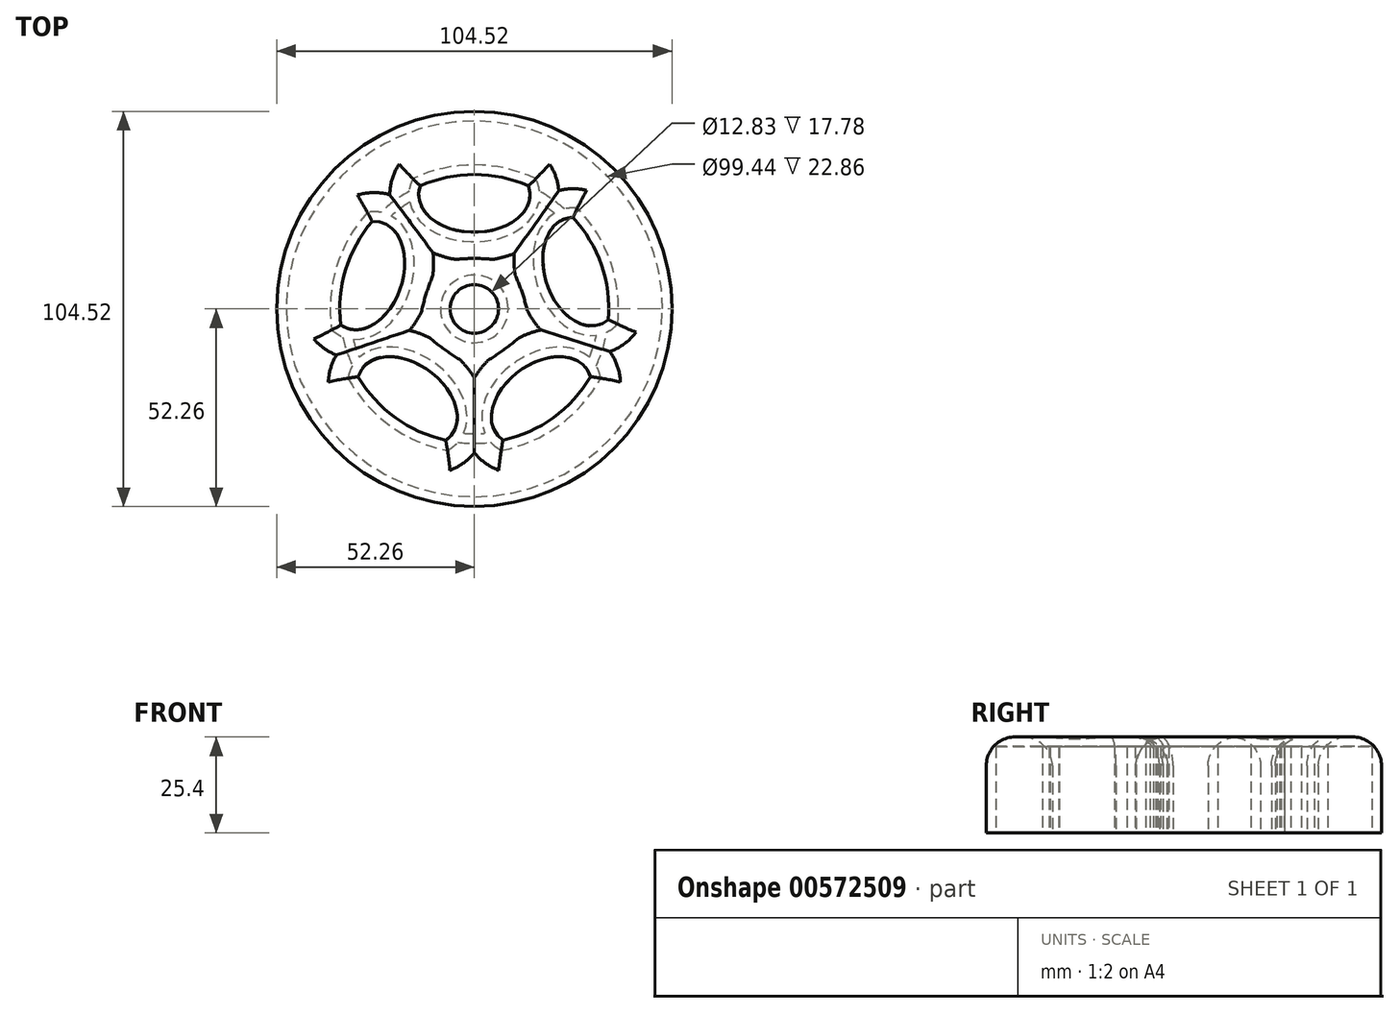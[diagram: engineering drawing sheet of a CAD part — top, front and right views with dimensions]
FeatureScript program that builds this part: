
annotation { "Feature Type Name" : "Feature", "Feature Type Description" : "" }
export const myFeature = defineFeature(function(context is Context, id is Id, definition is map)
    precondition{}
    {
        {
            var Q0;
            Q0=qCreatedBy(makeId("Top.planeOp"),FACE);
            var sketch = newSketch(context, id + "F0", { "sketchPlane" : qUnion([Q0])});
            skCircle(sketch, "E0", {"center": v(0, 0) * mm, "radius": 52.26 * mm});
            skCircle(sketch, "E1", {"center": v(0, 0) * mm, "radius": 6.41 * mm});
            skEllipse(sketch, "E2", {"center": v(0, 30.2) * mm, "majorRadius": 14.73 * mm, "minorRadius": 9.91 * mm, "majorAxis": v(1, 0)});
            skEllipse(sketch, "E3", {"center": v(28.56, 9.84) * mm, "majorRadius": 14.73 * mm, "minorRadius": 9.91 * mm, "majorAxis": v(0.3, -0.95)});
            skEllipse(sketch, "E4", {"center": v(-17.75, -24.43) * mm, "majorRadius": 14.73 * mm, "minorRadius": 9.91 * mm, "majorAxis": v(-0.8, 0.59)});
            skEllipse(sketch, "E5", {"center": v(-28.89, 8.83) * mm, "majorRadius": 14.73 * mm, "minorRadius": 9.91 * mm, "majorAxis": v(0.3, 0.95)});
            skEllipse(sketch, "E6", {"center": v(17.75, -24.43) * mm, "majorRadius": 14.73 * mm, "minorRadius": 9.91 * mm, "majorAxis": v(-0.8, -0.59)});
            skPoint(sketch, "E7.9.internal.snap0", {"position": v(-24.34, 22.84) * mm});
            skCircle(sketch, "E8", {"center": v(0, 0) * mm, "radius": 35.56 * mm});
            skLineSegment(sketch, "E9", {"start": v(0, 16.88) * mm, "end": v(0, 10.38) * mm});
            skLineSegment(sketch, "E10", {"start": v(17.66, 4.8) * mm, "end": v(8.6, 1.56) * mm});
            skLineSegment(sketch, "E11", {"start": v(10.52, -14.87) * mm, "end": v(4.69, -7.91) * mm});
            skLineSegment(sketch, "E12", {"start": v(-9, -14.74) * mm, "end": v(-4.03, -7.91) * mm});
            skLineSegment(sketch, "E13", {"start": v(-16.88, 4.25) * mm, "end": v(-8.55, 1.56) * mm});
            skSolve(sketch);
        }
        {
            var Q0;
            Q0=makeQuery(id+"F0.imprint","IMPRINT",FACE,{"disambiguationData":[TD([[makeQuery(id+"F0.imprint","IMPRINT",EDGE,{"derivedFrom":sQuery(id+"F0.wireOp",EDGE,"E1")}),-1.0]])]});
            extrude(context, id + "F1", {"entities" : qUnion([Q0]), "depth" : 25.4 * mm, "offsetDistance" : 25.4 * mm});
        }
        {
            var Q0;
            Q0=makeQuery(id+"F1.opExtrude","CAP_FACE",FACE,{"disambiguationData":[OSD([sQuery(id+"F0.wireOp",EDGE,"E1"),sQuery(id+"F0.wireOp",EDGE,"E2"),sQuery(id+"F0.wireOp",EDGE,"E3"),sQuery(id+"F0.wireOp",EDGE,"E4"),sQuery(id+"F0.wireOp",EDGE,"E5"),sQuery(id+"F0.wireOp",EDGE,"E6"),sQuery(id+"F0.wireOp",EDGE,"E8")])],"isStart":true});
            shell(context, id + "F2", {"entities" : qUnion([Q0]), "thickness" : 2.54 * mm});
        }
        {
            var Q0;
            Q0 = qSketchRegion(id + "F0", true);
            var Q1;
            {var subQ0=sQuery(id+"F0.wireOp",EDGE,"E8");var subQ1=sQuery(id+"F0.wireOp",EDGE,"E4");var subQ2=makeQuery(id+"F0.imprint","INTERSECT",VERTEX,{"disambiguationData":[OD(0.0)],"derivedFrom":[subQ1,subQ0]});Q1=makeQuery(id+"F0.imprint","IMPRINT",FACE,{"disambiguationData":[TD([[makeQuery(id+"F0.imprint","IMPRINT",EDGE,{"disambiguationData":[TD([[subQ2,-1.0]])],"derivedFrom":subQ1}),1.0]])]});}
            var Q2;
            {var subQ0=sQuery(id+"F0.wireOp",EDGE,"E8");var subQ1=sQuery(id+"F0.wireOp",EDGE,"E6");var subQ2=makeQuery(id+"F0.imprint","INTERSECT",VERTEX,{"disambiguationData":[OD(0.0)],"derivedFrom":[subQ1,subQ0]});Q2=makeQuery(id+"F0.imprint","IMPRINT",FACE,{"disambiguationData":[TD([[makeQuery(id+"F0.imprint","IMPRINT",EDGE,{"disambiguationData":[TD([[subQ2,-1.0]])],"derivedFrom":subQ1}),1.0]])]});}
            var Q3;
            {var subQ0=sQuery(id+"F0.wireOp",EDGE,"E8");var subQ1=sQuery(id+"F0.wireOp",EDGE,"E3");var subQ2=makeQuery(id+"F0.imprint","INTERSECT",VERTEX,{"disambiguationData":[OD(0.0)],"derivedFrom":[subQ1,subQ0]});Q3=makeQuery(id+"F0.imprint","IMPRINT",FACE,{"disambiguationData":[TD([[makeQuery(id+"F0.imprint","IMPRINT",EDGE,{"disambiguationData":[TD([[subQ2,1.0]])],"derivedFrom":subQ1}),1.0]])]});}
            var Q4;
            {var subQ0=sQuery(id+"F0.wireOp",EDGE,"E8");var subQ1=sQuery(id+"F0.wireOp",EDGE,"E2");var subQ2=makeQuery(id+"F0.imprint","INTERSECT",VERTEX,{"disambiguationData":[OD(0.0)],"derivedFrom":[subQ1,subQ0]});Q4=makeQuery(id+"F0.imprint","IMPRINT",FACE,{"disambiguationData":[TD([[makeQuery(id+"F0.imprint","IMPRINT",EDGE,{"disambiguationData":[TD([[subQ2,-1.0]])],"derivedFrom":subQ1}),1.0]])]});}
            var Q5;
            {var subQ0=sQuery(id+"F0.wireOp",EDGE,"E8");var subQ1=sQuery(id+"F0.wireOp",EDGE,"E5");var subQ2=makeQuery(id+"F0.imprint","INTERSECT",VERTEX,{"disambiguationData":[OD(0.0)],"derivedFrom":[subQ1,subQ0]});Q5=makeQuery(id+"F0.imprint","IMPRINT",FACE,{"disambiguationData":[TD([[makeQuery(id+"F0.imprint","IMPRINT",EDGE,{"disambiguationData":[TD([[subQ2,-1.0]])],"derivedFrom":subQ1}),1.0]])]});}
            extrude(context, id + "F3", {"entities" : qUnion([Q0, Q1, Q2, Q3, Q4, Q5]), "operationType" : NewBodyOperationType.ADD, "depth" : 25.4 * mm, "offsetDistance" : 25.4 * mm});
        }
        {
            var Q0;
            {var subQ0=sQuery(id+"F0.wireOp",EDGE,"E8");Q0=makeQuery(id+"F3.boolean.opBoolean","MERGE",FACE,{"derivedFrom":[makeQuery(id+"F1.opExtrude","CAP_FACE",FACE,{"disambiguationData":[OSD([sQuery(id+"F0.wireOp",EDGE,"E1"),sQuery(id+"F0.wireOp",EDGE,"E2"),sQuery(id+"F0.wireOp",EDGE,"E3"),sQuery(id+"F0.wireOp",EDGE,"E4"),sQuery(id+"F0.wireOp",EDGE,"E5"),sQuery(id+"F0.wireOp",EDGE,"E6"),subQ0])],"isStart":true}),makeQuery(id+"F3.opExtrude","CAP_FACE",FACE,{"disambiguationData":[OSD([sQuery(id+"F0.wireOp",EDGE,"E0"),subQ0])],"isStart":true})]});}
            shell(context, id + "F4", {"entities" : qUnion([Q0]), "thickness" : 2.54 * mm});
        }
        {
            var Q0;
            {var subQ0=sQuery(id+"F0.wireOp",EDGE,"E8");Q0=makeQuery(id+"F3.boolean.opBoolean","MERGE",FACE,{"derivedFrom":[makeQuery(id+"F1.opExtrude","CAP_FACE",FACE,{"disambiguationData":[OSD([sQuery(id+"F0.wireOp",EDGE,"E1"),sQuery(id+"F0.wireOp",EDGE,"E2"),sQuery(id+"F0.wireOp",EDGE,"E3"),sQuery(id+"F0.wireOp",EDGE,"E4"),sQuery(id+"F0.wireOp",EDGE,"E5"),sQuery(id+"F0.wireOp",EDGE,"E6"),subQ0])],"isStart":false}),makeQuery(id+"F3.opExtrude","CAP_FACE",FACE,{"disambiguationData":[OSD([sQuery(id+"F0.wireOp",EDGE,"E0"),subQ0])],"isStart":false})]});}
            fillet(context, id + "F5", {"entities" : qUnion([Q0]), "radius" : 7.62 * mm, "tangentPropagation" : true, "allowEdgeOverflow" : false});
        }
    });
